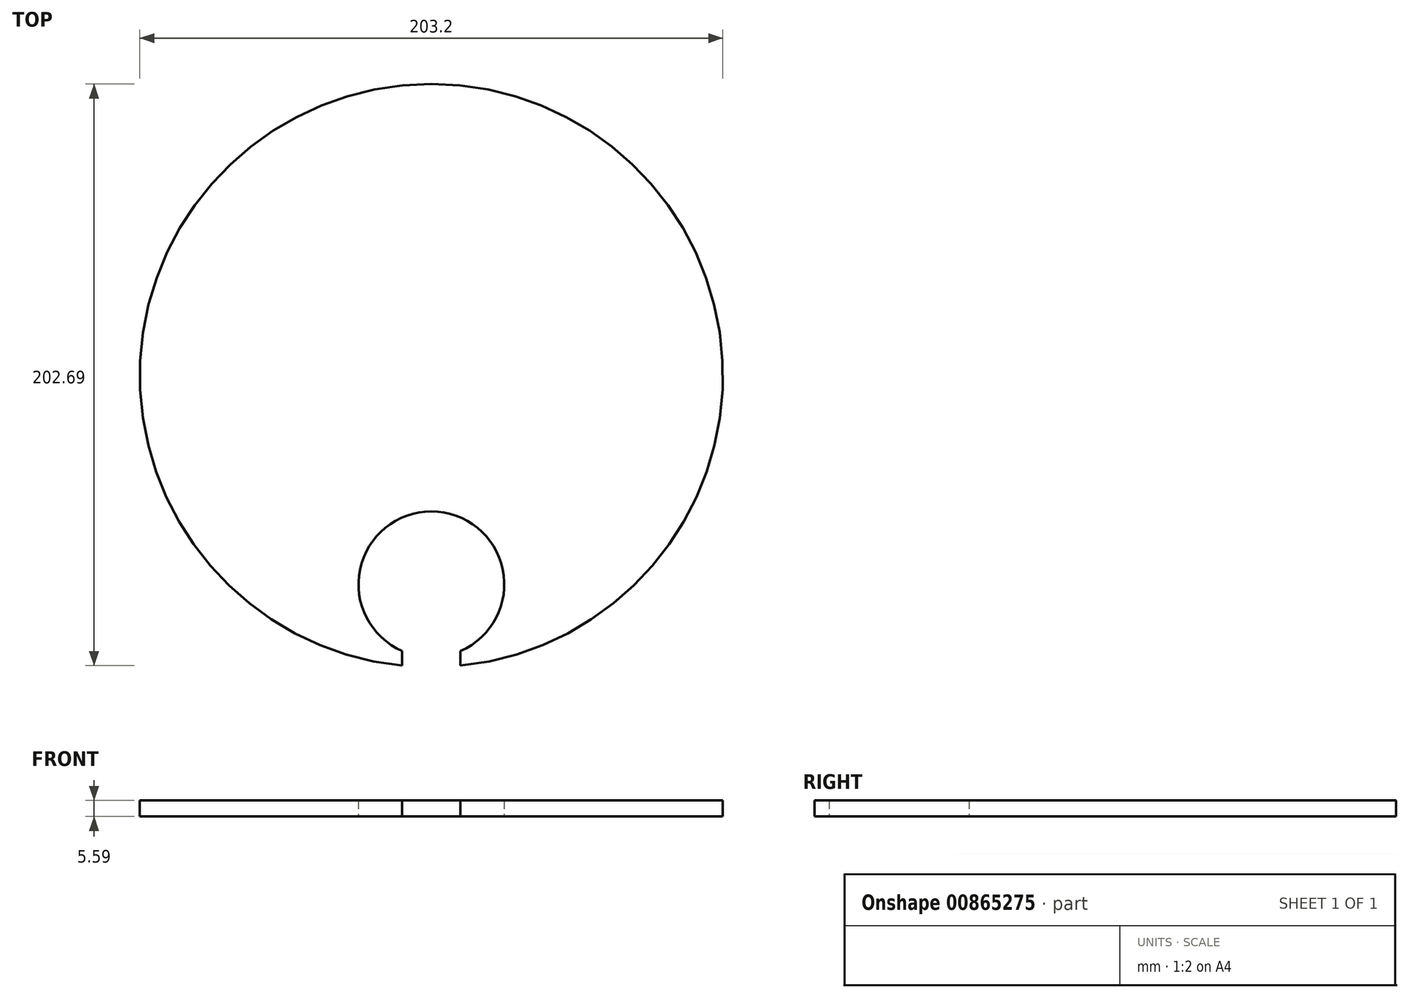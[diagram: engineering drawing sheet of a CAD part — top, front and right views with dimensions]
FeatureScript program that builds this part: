
annotation { "Feature Type Name" : "Feature", "Feature Type Description" : "" }
export const myFeature = defineFeature(function(context is Context, id is Id, definition is map)
    precondition{}
    {
        {
            var Q0;
            Q0=qCreatedBy(makeId("Top.planeOp"),FACE);
            var sketch = newSketch(context, id + "F0", { "sketchPlane" : qUnion([Q0])});
            skCircle(sketch, "E0", {"center": v(0, 0) * mm, "radius": 101.6 * mm});
            skLineSegment(sketch, "E1", {"start": v(-10.16, -101.1) * mm, "end": v(10.16, -101.1) * mm});
            skLineSegment(sketch, "E2", {"start": v(0, -101.1) * mm, "end": v(0, -96.01) * mm});
            skLineSegment(sketch, "E3.bottom", {"start": v(-10.16, -96.01) * mm, "end": v(10.16, -96.01) * mm});
            skLineSegment(sketch, "E3.left", {"start": v(-10.16, -96.01) * mm, "end": v(-10.16, -101.1) * mm});
            skLineSegment(sketch, "E3.right", {"start": v(10.16, -96.01) * mm, "end": v(10.16, -101.1) * mm});
            skArc(sketch, "E4", {"start": v(10.16, -96.01) * mm, "mid": v(0, -47.33) * mm, "end": v(-10.16, -96.01) * mm});
            skSolve(sketch);
        }
        {
            var Q0;
            {var subQ0=sQuery(id+"F0.wireOp",EDGE,"E3.left");Q0=makeQuery(id+"F0.imprint","IMPRINT",FACE,{"disambiguationData":[TD([[makeQuery(id+"F0.imprint","IMPRINT",EDGE,{"derivedFrom":subQ0}),-1.0]])]});}
            extrude(context, id + "F1", {"entities" : qUnion([Q0]), "depth" : 5.6 * mm, "offsetDistance" : 25.4 * mm});
        }
    });
